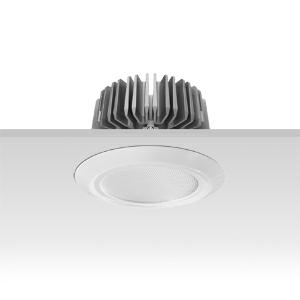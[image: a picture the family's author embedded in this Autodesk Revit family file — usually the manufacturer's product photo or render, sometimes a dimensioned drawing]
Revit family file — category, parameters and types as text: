
# Revit family: 3f_filippi_-_3f_reno_bianco_ampio_3f_filippi_-_30379_a01035_-_3f_reno_150_wh_2000-930_dali_wide___vs_wh_1189
name_source: partatom
category: Lighting Fixtures
units: mm (PartAtom-declared; Revit-internal decimal feet)

## family parameters
Cut with Voids When Loaded = No
Host = Face
Light Source = No
Part Type = Normal
Room Calculation Point = No
Round Connector Dimension = Use Diameter
Shared = No

## types (1)
- 3F Filippi - 3F Reno Bianco Ampio (1 x LED, 1636 lm, 24 W, 3000 K)
    Apparent Load = 24 VA
    Approval mark = CE
    CIE Flux Codes = 74 93 99 100 100
    Color Rendering = 90
    Color Temperature = 3000 K
    Control Gear = Electronic transformer
    Default Elevation = 1800 mm
    Description = ILLUMINOTECHNICAL
Luminous efficiency 100% (DLOR 100%, ULOR 0%).
Initial luminous flux of the luminaire 1636 lm.
Direct symmetric wide distribution.
Installation Interdistance Transv.D = 1.12 x hu - Long.D = 1.11 x hu.
Tabular UGR (CIE 117 - 4H-8H; S=0.25H; 70/50/20): RUG 22.7 - 22.5.
Beam angle: 74° - 73°.
Luminous efficacy 68 lm/W.
Lifetime (L90/B10): 30000 h. (tq+25°C)
Lifetime (L85/B10): 50000 h. (tq+25°C)
Lifetime (L70/B10): 80000 h. (tq+25°C)
Sudden decreased luminous flux after 50000 hours: 0% (C0).
Photobiological safety in compliance with IEC/TR 62778: RG0 risk exempt, (IEC 62471).
In compliance with IEC/EN 62722-2-1 - IEC/EN 62717 standards.

SOURCE
Compact LED module 2000/930.
Energy efficiency class (UE 2019/2020 - UE 2019/2015): E.
CIE 13.3 Colour rendering index: CRI >90 (R9 >50%).
IES TM-30 Fidelity Index: Rf = 92 Rg = 101.
CCT nominal colour temperature 3000 K.
Colour initial tolerance (MacAdam): SDCM 3.
Zhaga Book 3 compliant.

MECHANICAL
Passive heat dissipator in die-casting aluminium, oversized, for optimum thermal management of the LED module.
Parabolic element with graduated/concentric rings in white polycarbonate.
Transparent external lens with glossy and satin differentiated surfaces, with a cooling and anti-insect system in methacrylate (PMMA).
Fastening spring clips in stainless steel.
Dimensions: diameter 176 mm, height 111 mm. Weight 0.89 kg.
IP44 protection degree for exposed part, IP20 for recessed part.
Mechanical strength to impacts IK06 (1 joule).
Glow-wire test resistance 650°C.

ELECTRICAL
Wiring on a separate unit.
Halogen Free DALI-2 DATI (Parts 251, 252, 253), PUSH-DIM, electronic wiring 230V-50/60Hz, power factor 0.95 at full load, THD <25%, constant output current, SELV, class II, 1 driver, 1 DALI addresse.
Power of the luminaire 24 W.
ENEC - CE.
SAFE FLICKER: PstLM=<1 and SVM=<0.4 (IEC TR 61547-1 and IEC TR 63158), to ensure a more comfortable and safe light.
Luminaire compliant with EN 60598-2-22 for power supply from a centralised emergency system CPSS (Central Power Supply System), not incorporated in the luminaire - high risk areas excluded. The default power and flux are 100% in AC and 100% in DC.
Ambient temperature from 0°C to +25°C.
Temperature class T6 max 85°C.
Relative humidity UR: <85%.

INSTALLATION
Pull-up recessed fitting.
False ceiling carving: 150 mm.
All accessories dedicated to this product are available on the Catalog and on our website www.3F-Filippi.com.

ACCESSORIES
A01035 - Anti-glare microprismatic VS moulded glass, tempered, not flammable, locked and in line with the trim, in white polycarbonate.

APPLICATIONS
Environments: architectural, commercial, exhibition areas, transit areas, corridors, shops, display windows, service areas.
In false ceilings with narrow voids.

LIGHT MANAGEMENT
Recommended minimum setting: 10%.
The luminaire, equipped with (DALI-2 DATI) driver, can be controlled manually with 3F Easy Dim technology or automatically/manually with wired or wireless DALI/D2D control systems.
The D2D driver guarantees interoperability with other devices with the same certification by making the following information available:
Device Data (Part 251), Energy Report (Part 252), Diagnosis & Maintenance (Part 253).
In electrical systems without a regulation system (manual or automatic) and DALI bus, a suitable jumper must be made on the DA-DA terminals of the appliance.

WARNING
Luminaire designed for disposal/recycling at end-of-life.
Replaceable (LED only) light source by a professional. Replaceable control gear by a professional.
    Height = 0 mm  [stored 0 ft]
    Lamp = 1 x LED
    Lamp Light Flux = 1636 lm
    Lamp Power = 24 W
    Lamp count = 1
    Length = 176 mm
    Lifetime = 50000 h
    Luminous efficacy = 68 lm/W
    Manufacturer = 3F Filippi
    ModVariant = No
    Model = 3F Filippi - 30379+A01035 - 3F Reno 150 WH 2000-930 DALI WIDE + VS WH
    Mounting Place = Ceiling
    Mounting Type = Recessed
    Number of Poles = 1
    OnlyDefault = Yes
    Power Factor = 1
    Product Name = 3F Filippi - 3F Reno Bianco Ampio
    Product group = recessed luminaire
    ProductGroupID = 4
    Protection Class = Protection class II
    Protection Degree = IP 20
    RLX_Detail_Level = 1
    RLX_Emergency_Light_Flux = 0 lm
    RLX_Emergency_Type = 0
    RLX_Emergency_Type_DB = No
    RlxData = <blob elided: 85645 chars, md5=1cb48fbb>
    Socket = socket
    Standby Power = 0 W
    System Light Flux = 1636 lm
    System Power = 24 W
    Type Comments = Product without accessories
    Type Image = 3ffilippi_3f_reno_150_wh_vs_smp.jpg
    URL = http://relux.com
    VarID = ---
    Voltage = 0 V
    Weight = 0.00 kg
    Width = 0 mm  [stored 0 ft]

note: [stored X ft] marks values corroborated as IEEE doubles in the binary element streams (Revit-internal decimal feet)

## geometry (parser evidence)
native form markers: Blend x4, Sweep x11
no freeform markers — native parametric forms only
